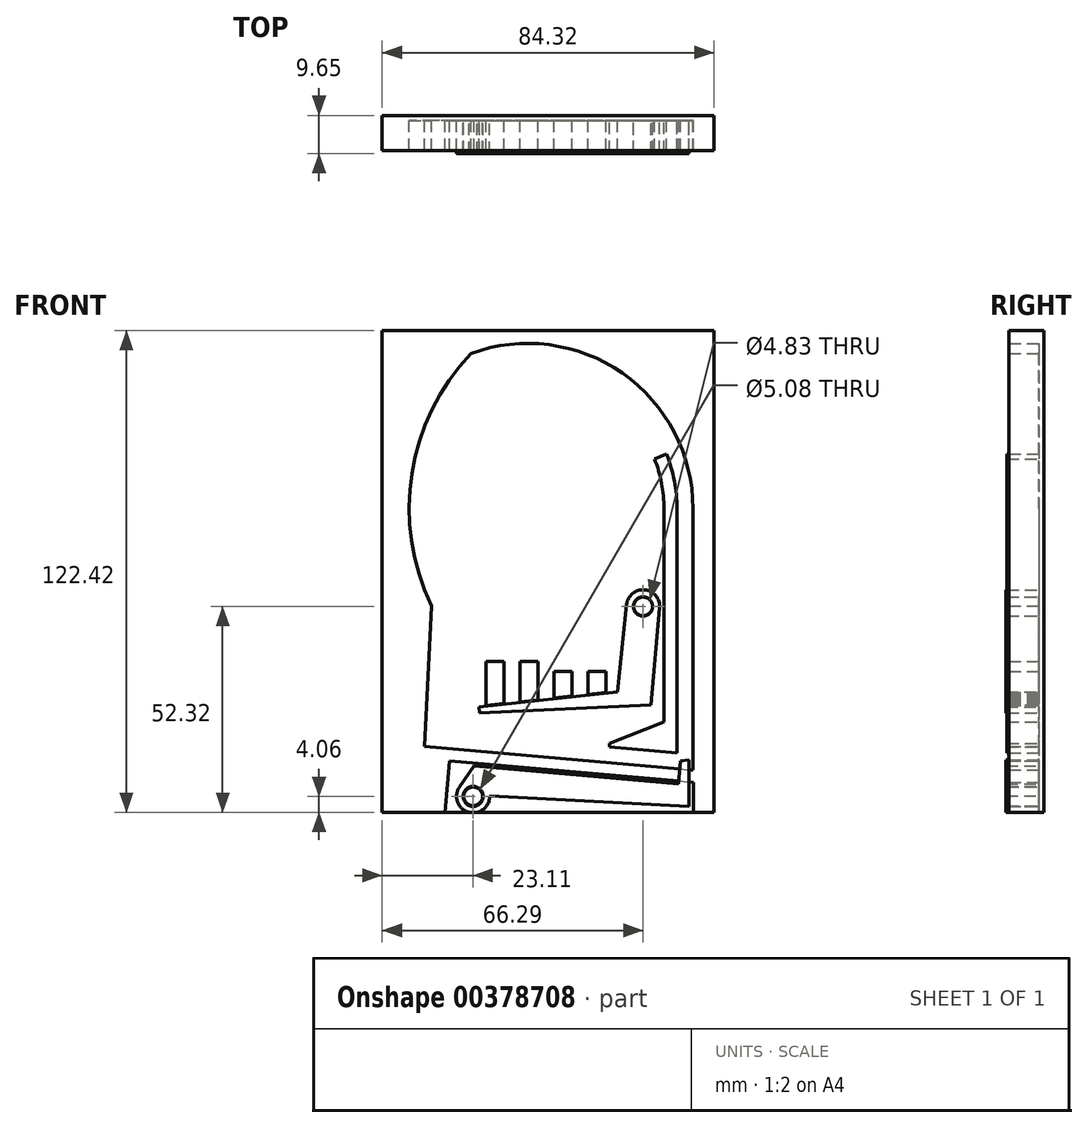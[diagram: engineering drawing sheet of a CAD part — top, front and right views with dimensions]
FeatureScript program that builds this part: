
annotation { "Feature Type Name" : "Feature", "Feature Type Description" : "" }
export const myFeature = defineFeature(function(context is Context, id is Id, definition is map)
    precondition{}
    {
        {
            var Q0;
            Q0=qCreatedBy(makeId("Front.planeOp"),FACE);
            var sketch = newSketch(context, id + "F0", { "sketchPlane" : qUnion([Q0])});
            skLineSegment(sketch, "E0.bottom", {"start": v(44.45, 63.5) * mm, "end": v(-44.45, 63.5) * mm});
            skLineSegment(sketch, "E0.top", {"start": v(44.45, -63.5) * mm, "end": v(-44.45, -63.5) * mm});
            skLineSegment(sketch, "E0.left", {"start": v(44.45, 63.5) * mm, "end": v(44.45, -63.5) * mm});
            skLineSegment(sketch, "E0.right", {"start": v(-44.45, 63.5) * mm, "end": v(-44.45, -63.5) * mm});
            skPoint(sketch, "E0.middle", {"position": v(0, 0) * mm});
            skLineSegment(sketch, "E1", {"start": v(-29.21, -42.66) * mm, "end": v(34.79, -48.26) * mm});
            skLineSegment(sketch, "E2", {"start": v(34.79, -48.26) * mm, "end": v(34.79, 15.95) * mm});
            skArc(sketch, "E3", {"start": v(34.79, 15.95) * mm, "mid": v(17.9, 48.57) * mm, "end": v(-18.48, 53.63) * mm});
            skArc(sketch, "E4", {"start": v(-18.48, 53.63) * mm, "mid": v(-32.67, 24.06) * mm, "end": v(-27.54, -8.34) * mm});
            skLineSegment(sketch, "E5", {"start": v(-27.54, -8.34) * mm, "end": v(-29.21, -42.66) * mm});
            skLineSegment(sketch, "E6", {"start": v(-17.78, -22.86) * mm, "end": v(-17.78, -30.48) * mm});
            skLineSegment(sketch, "E7", {"start": v(-9.14, -22.86) * mm, "end": v(-9.14, -33.34) * mm});
            skLineSegment(sketch, "E8", {"start": v(-0.5, -22.86) * mm, "end": v(-0.5, -32.39) * mm});
            skLineSegment(sketch, "E9", {"start": v(8.13, -22.86) * mm, "end": v(8.13, -31.43) * mm});
            skLineSegment(sketch, "E10", {"start": v(16.76, -22.86) * mm, "end": v(16.76, -30.48) * mm});
            skCircle(sketch, "E11", {"center": v(16.76, -30.48) * mm, "radius": 1.59 * mm});
            skLineSegment(sketch, "E12", {"start": v(16.76, -30.48) * mm, "end": v(-17.78, -34.3) * mm});
            skLineSegment(sketch, "E13", {"start": v(-17.78, -34.3) * mm, "end": v(-17.78, -30.48) * mm});
            skLineSegment(sketch, "E14", {"start": v(-28, -37.08) * mm, "end": v(-29.8, -37.08) * mm});
            skLineSegment(sketch, "E15", {"start": v(-17.78, -37.61) * mm, "end": v(26.76, -32.7) * mm});
            skLineSegment(sketch, "E16", {"start": v(26.76, -32.7) * mm, "end": v(24.13, -8.89) * mm});
            skLineSegment(sketch, "E17", {"start": v(-21.28, -49.63) * mm, "end": v(34.73, -55.5) * mm});
            skLineSegment(sketch, "E18", {"start": v(34.73, -55.5) * mm, "end": v(49.3, -48.12) * mm});
            skPoint(sketch, "E19", {"position": v(-19.05, -57.15) * mm});
            skSolve(sketch);
        }
        {
            var Q0;
            Q0=qCreatedBy(makeId("Front.planeOp"),FACE);
            cPlane(context, id + "F1", {"entities" : qUnion([Q0]), "cplaneType" : CPlaneType.OFFSET, "offset" : 6.35 * mm, "oppositeDirection" : true, "width" : 152.4 * mm, "height" : 152.4 * mm});
        }
        {
            var Q0;
            Q0=qCreatedBy(id+"F1.planeOp",FACE);
            var sketch = newSketch(context, id + "F2", { "sketchPlane" : qUnion([Q0])});
            skLineSegment(sketch, "E20.bottom", {"start": v(-42.16, 61.21) * mm, "end": v(42.16, 61.21) * mm});
            skLineSegment(sketch, "E20.top", {"start": v(-42.16, -61.21) * mm, "end": v(42.16, -61.21) * mm});
            skLineSegment(sketch, "E20.left", {"start": v(-42.16, 61.21) * mm, "end": v(-42.16, -61.21) * mm});
            skLineSegment(sketch, "E20.right", {"start": v(42.16, 61.21) * mm, "end": v(42.16, -61.21) * mm});
            skPoint(sketch, "E20.middle", {"position": v(0, 0) * mm});
            skLineSegment(sketch, "E21.0", {"start": v(44.45, 63.5) * mm, "end": v(-44.45, 63.5) * mm});
            skLineSegment(sketch, "E22.0", {"start": v(-44.45, 63.5) * mm, "end": v(-44.45, -63.5) * mm});
            skLineSegment(sketch, "E23.0", {"start": v(44.45, -63.5) * mm, "end": v(-44.45, -63.5) * mm});
            skLineSegment(sketch, "E24.0", {"start": v(44.45, 63.5) * mm, "end": v(44.45, -63.5) * mm});
            skSolve(sketch);
        }
        {
            var Q0;
            Q0=makeQuery(id+"F2.imprint","IMPRINT",FACE,{"disambiguationData":[TD([[makeQuery(id+"F2.imprint","IMPRINT",EDGE,{"derivedFrom":sQuery(id+"F2.wireOp",EDGE,"E20.bottom")}),-1.0]])]});
            extrude(context, id + "F3", {"entities" : qUnion([Q0]), "depth" : 1.27 * mm});
        }
        {
            var Q0;
            Q0=qCreatedBy(id+"F1.planeOp",FACE);
            var sketch = newSketch(context, id + "F4", { "sketchPlane" : qUnion([Q0])});
            skLineSegment(sketch, "E25.0", {"start": v(34.79, -48.26) * mm, "end": v(34.79, 15.95) * mm, "construction": true});
            skArc(sketch, "E26.0", {"start": v(34.79, 15.95) * mm, "mid": v(17.9, 48.57) * mm, "end": v(-18.48, 53.63) * mm, "construction": true});
            skArc(sketch, "E27.0", {"start": v(-18.48, 53.63) * mm, "mid": v(-32.67, 24.06) * mm, "end": v(-27.54, -8.34) * mm, "construction": true});
            skLineSegment(sketch, "E28.0", {"start": v(-27.54, -8.34) * mm, "end": v(-29.21, -42.66) * mm, "construction": true});
            skLineSegment(sketch, "E29.0", {"start": v(-29.21, -42.66) * mm, "end": v(34.79, -48.26) * mm, "construction": true});
            skLineSegment(sketch, "E30.0", {"start": v(44.45, 63.5) * mm, "end": v(-44.45, 63.5) * mm, "construction": true});
            skLineSegment(sketch, "E31.0", {"start": v(42.16, 61.21) * mm, "end": v(42.16, -61.21) * mm});
            skLineSegment(sketch, "E32.0", {"start": v(-42.16, 61.21) * mm, "end": v(42.16, 61.21) * mm});
            skLineSegment(sketch, "E33.0", {"start": v(-42.16, 61.21) * mm, "end": v(-42.16, -61.21) * mm});
            skLineSegment(sketch, "E34.0", {"start": v(-42.16, -61.21) * mm, "end": v(42.16, -61.21) * mm});
            skArc(sketch, "E35.0", {"start": v(36.82, 15.95) * mm, "mid": v(18.87, 50.38) * mm, "end": v(-19.63, 55.38) * mm});
            skLineSegment(sketch, "E35.1", {"start": v(36.82, -50.48) * mm, "end": v(36.82, 15.95) * mm});
            skArc(sketch, "E35.2", {"start": v(-19.63, 55.38) * mm, "mid": v(-34.6, 24.86) * mm, "end": v(-29.6, -8.76) * mm});
            skLineSegment(sketch, "E35.3", {"start": v(-29.6, -8.76) * mm, "end": v(-31.33, -44.51) * mm});
            skLineSegment(sketch, "E35.4", {"start": v(-31.33, -44.51) * mm, "end": v(36.82, -50.48) * mm});
            skLineSegment(sketch, "E36", {"start": v(-26.22, -61.21) * mm, "end": v(-25.07, -48.12) * mm});
            skLineSegment(sketch, "E37", {"start": v(-25.07, -48.12) * mm, "end": v(36.94, -53.55) * mm});
            skLineSegment(sketch, "E38", {"start": v(36.94, -53.55) * mm, "end": v(36.94, -61.21) * mm});
            skSolve(sketch);
        }
        {
            var Q0;
            {var subQ1=sQuery(id+"F4.wireOp",EDGE,"E31.0");Q0=makeQuery(id+"F4.imprint","IMPRINT",FACE,{"disambiguationData":[TD([[makeQuery(id+"F4.imprint","IMPRINT",EDGE,{"derivedFrom":subQ1}),-1.0]])]});}
            extrude(context, id + "F5", {"entities" : qUnion([Q0]), "operationType" : NewBodyOperationType.ADD, "depth" : 8.9 * mm});
        }
        {
            var Q0;
            Q0=qCreatedBy(id+"F1.planeOp",FACE);
            var sketch = newSketch(context, id + "F6", { "sketchPlane" : qUnion([Q0])});
            skArc(sketch, "E39.0", {"start": v(32.76, 15.95) * mm, "mid": v(32.1, 23.01) * mm, "end": v(30.12, 29.84) * mm});
            skLineSegment(sketch, "E39.1", {"start": v(32.76, -46.04) * mm, "end": v(32.76, 15.95) * mm});
            skPoint(sketch, "E40.0", {"position": v(24.13, -8.89) * mm});
            skCircle(sketch, "E41", {"center": v(24.13, -8.89) * mm, "radius": 2.39 * mm});
            skArc(sketch, "E42.0", {"start": v(29.46, 15.95) * mm, "mid": v(28.85, 22.4) * mm, "end": v(27.05, 28.63) * mm});
            skLineSegment(sketch, "E42.1", {"start": v(29.46, -45.75) * mm, "end": v(29.46, 15.95) * mm});
            skLineSegment(sketch, "E43", {"start": v(-5.18, 15.95) * mm, "end": v(30.12, 29.84) * mm});
            skLineSegment(sketch, "E44.0", {"start": v(15.56, -44.54) * mm, "end": v(32.76, -46.04) * mm});
            skLineSegment(sketch, "E45", {"start": v(15.56, -44.54) * mm, "end": v(15.63, -43.75) * mm});
            skLineSegment(sketch, "E46", {"start": v(15.63, -43.75) * mm, "end": v(29.46, -38.18) * mm});
            skPoint(sketch, "E47.0", {"position": v(-19.05, -57.15) * mm});
            skCircle(sketch, "E48", {"center": v(-19.05, -57.15) * mm, "radius": 2.39 * mm});
            skSolve(sketch);
        }
        {
            var Q0;
            {var subQ4=sQuery(id+"F6.wireOp",EDGE,"E45");Q0=makeQuery(id+"F6.imprint","IMPRINT",FACE,{"disambiguationData":[TD([[makeQuery(id+"F6.imprint","IMPRINT",EDGE,{"derivedFrom":subQ4}),-1.0]])]});}
            var Q1;
            {var subQ6=sQuery(id+"F6.wireOp",EDGE,"E39.0");Q1=makeQuery(id+"F6.imprint","IMPRINT",FACE,{"disambiguationData":[TD([[makeQuery(id+"F6.imprint","IMPRINT",EDGE,{"derivedFrom":subQ6}),1.0]])]});}
            var Q2;
            Q2=makeQuery(id+"F6.imprint","IMPRINT",FACE,{"disambiguationData":[TD([[makeQuery(id+"F6.imprint","IMPRINT",EDGE,{"derivedFrom":sQuery(id+"F6.wireOp",EDGE,"E41")}),1.0]])]});
            var Q3;
            Q3=makeQuery(id+"F6.imprint","IMPRINT",FACE,{"disambiguationData":[TD([[makeQuery(id+"F6.imprint","IMPRINT",EDGE,{"derivedFrom":sQuery(id+"F6.wireOp",EDGE,"E48")}),1.0]])]});
            extrude(context, id + "F7", {"entities" : qUnion([Q0, Q1, Q2, Q3]), "operationType" : NewBodyOperationType.ADD, "depth" : 9.4 * mm});
        }
        {
            var Q0;
            Q0=qCreatedBy(id+"F1.planeOp",FACE);
            var sketch = newSketch(context, id + "F8", { "sketchPlane" : qUnion([Q0])});
            skLineSegment(sketch, "E49.0", {"start": v(16.76, -22.86) * mm, "end": v(16.76, -30.48) * mm, "construction": true});
            skLineSegment(sketch, "E50.0", {"start": v(8.13, -22.86) * mm, "end": v(8.13, -31.43) * mm, "construction": true});
            skLineSegment(sketch, "E51.0", {"start": v(-0.5, -22.86) * mm, "end": v(-0.5, -32.39) * mm, "construction": true});
            skLineSegment(sketch, "E52.0", {"start": v(-9.14, -22.86) * mm, "end": v(-9.14, -33.34) * mm, "construction": true});
            skPoint(sketch, "E53.0", {"position": v(-17.78, -26.67) * mm});
            skLineSegment(sketch, "E54.0", {"start": v(-17.78, -22.86) * mm, "end": v(-17.78, -30.48) * mm, "construction": true});
            skLineSegment(sketch, "E55.0", {"start": v(-17.78, -34.3) * mm, "end": v(-17.78, -30.48) * mm, "construction": true});
            skLineSegment(sketch, "E56.0", {"start": v(14.73, -30.7) * mm, "end": v(10.16, -31.2) * mm});
            skLineSegment(sketch, "E57.0", {"start": v(-19.81, -34.51) * mm, "end": v(-19.81, -33.02) * mm});
            skLineSegment(sketch, "E57.1", {"start": v(-19.81, -25.4) * mm, "end": v(-19.81, -33.02) * mm});
            skLineSegment(sketch, "E58.0", {"start": v(-15.75, -34.07) * mm, "end": v(-15.75, -33.02) * mm});
            skLineSegment(sketch, "E58.1", {"start": v(-15.75, -22.86) * mm, "end": v(-15.75, -33.02) * mm});
            skLineSegment(sketch, "E59.0", {"start": v(-11.18, -22.86) * mm, "end": v(-11.18, -33.56) * mm});
            skLineSegment(sketch, "E60.0", {"start": v(-7.11, -22.86) * mm, "end": v(-7.11, -33.11) * mm});
            skArc(sketch, "E61.0", {"start": v(-19.63, 55.38) * mm, "mid": v(-34.6, 24.86) * mm, "end": v(-29.6, -8.76) * mm});
            skLineSegment(sketch, "E61.1", {"start": v(-30.97, -36.98) * mm, "end": v(-31.33, -44.51) * mm});
            skLineSegment(sketch, "E61.2", {"start": v(-31.33, -44.51) * mm, "end": v(36.82, -50.48) * mm});
            skLineSegment(sketch, "E61.3", {"start": v(-29.6, -8.76) * mm, "end": v(-30.97, -36.98) * mm});
            skLineSegment(sketch, "E61.4", {"start": v(36.82, -50.48) * mm, "end": v(36.82, 15.95) * mm});
            skArc(sketch, "E61.5", {"start": v(36.82, 15.95) * mm, "mid": v(18.87, 50.38) * mm, "end": v(-19.63, 55.38) * mm});
            skLineSegment(sketch, "E62.0", {"start": v(-2.54, -22.86) * mm, "end": v(-2.54, -32.6) * mm});
            skLineSegment(sketch, "E63.0", {"start": v(1.52, -25.4) * mm, "end": v(1.52, -32.16) * mm});
            skLineSegment(sketch, "E64.0", {"start": v(6.1, -25.4) * mm, "end": v(6.1, -31.66) * mm});
            skLineSegment(sketch, "E65.0", {"start": v(10.16, -25.4) * mm, "end": v(10.16, -31.2) * mm});
            skLineSegment(sketch, "E66.0", {"start": v(14.73, -25.4) * mm, "end": v(14.73, -30.7) * mm});
            skLineSegment(sketch, "E67.0", {"start": v(18.8, -25.4) * mm, "end": v(18.8, -30.26) * mm});
            skLineSegment(sketch, "E68", {"start": v(-7.11, -22.86) * mm, "end": v(-2.54, -22.86) * mm});
            skLineSegment(sketch, "E69", {"start": v(1.52, -25.4) * mm, "end": v(6.1, -25.4) * mm});
            skLineSegment(sketch, "E70", {"start": v(10.16, -25.4) * mm, "end": v(14.73, -25.4) * mm});
            skPoint(sketch, "E71.orphan", {"position": v(-17.78, -34.3) * mm});
            skLineSegment(sketch, "E72.trimOffspring", {"start": v(-11.18, -33.56) * mm, "end": v(-15.75, -34.07) * mm});
            skLineSegment(sketch, "E73.trimOffspring", {"start": v(-2.54, -32.6) * mm, "end": v(-7.11, -33.11) * mm});
            skLineSegment(sketch, "E74.trimOffspring", {"start": v(6.1, -31.66) * mm, "end": v(1.52, -32.16) * mm});
            skPoint(sketch, "E75.orphan", {"position": v(16.76, -30.48) * mm});
            skLineSegment(sketch, "E76", {"start": v(-15.75, -22.86) * mm, "end": v(-11.18, -22.86) * mm});
            skSolve(sketch);
        }
        {
            var Q0;
            Q0=makeQuery(id+"F8.imprint","IMPRINT",FACE,{"disambiguationData":[TD([[makeQuery(id+"F8.imprint","IMPRINT",EDGE,{"derivedFrom":sQuery(id+"F8.wireOp",EDGE,"E58.0")}),-1.0]])]});
            var Q1;
            Q1=makeQuery(id+"F8.imprint","IMPRINT",FACE,{"disambiguationData":[TD([[makeQuery(id+"F8.imprint","IMPRINT",EDGE,{"derivedFrom":sQuery(id+"F8.wireOp",EDGE,"E60.0")}),1.0]])]});
            var Q2;
            Q2=makeQuery(id+"F8.imprint","IMPRINT",FACE,{"disambiguationData":[TD([[makeQuery(id+"F8.imprint","IMPRINT",EDGE,{"derivedFrom":sQuery(id+"F8.wireOp",EDGE,"E63.0")}),1.0]])]});
            var Q3;
            Q3=makeQuery(id+"F8.imprint","IMPRINT",FACE,{"disambiguationData":[TD([[makeQuery(id+"F8.imprint","IMPRINT",EDGE,{"derivedFrom":sQuery(id+"F8.wireOp",EDGE,"E56.0")}),-1.0]])]});
            extrude(context, id + "F9", {"entities" : qUnion([Q0, Q1, Q2, Q3]), "operationType" : NewBodyOperationType.ADD, "depth" : 8.9 * mm});
        }
        {
            var Q0;
            Q0=makeQuery(id+"F5.boolean.opBoolean","SPLIT",FACE,{"disambiguationData":[TD([makeQuery(id+"F5.opExtrude","SWEPT_FACE",FACE,{"disambiguationData":[OSD([sQuery(id+"F4.wireOp",EDGE,"E35.0")])]})])],"derivedFrom":makeQuery(id+"F3.opExtrude","CAP_FACE",FACE,{"disambiguationData":[OSD([sQuery(id+"F2.wireOp",EDGE,"E20.bottom"),sQuery(id+"F2.wireOp",EDGE,"E20.top"),sQuery(id+"F2.wireOp",EDGE,"E20.left"),sQuery(id+"F2.wireOp",EDGE,"E20.right")])],"isStart":false})});
            var sketch = newSketch(context, id + "F10", { "sketchPlane" : qUnion([Q0])});
            skCircle(sketch, "E77", {"center": v(24.13, -8.89) * mm, "radius": 2.41 * mm});
            skCircle(sketch, "E78", {"center": v(24.13, -8.89) * mm, "radius": 4.22 * mm});
            skLineSegment(sketch, "E79", {"start": v(19.93, -8.44) * mm, "end": v(17.59, -30.56) * mm});
            skLineSegment(sketch, "E80", {"start": v(17.59, -30.56) * mm, "end": v(-17.53, -34.43) * mm});
            skLineSegment(sketch, "E81", {"start": v(-17.53, -34.43) * mm, "end": v(-17.36, -36) * mm});
            skLineSegment(sketch, "E82", {"start": v(-17.36, -36) * mm, "end": v(26.18, -33.87) * mm});
            skLineSegment(sketch, "E83", {"start": v(26.18, -33.87) * mm, "end": v(28.33, -9.26) * mm});
            skLineSegment(sketch, "E84.0", {"start": v(-11.18, -33.56) * mm, "end": v(-15.75, -34.07) * mm});
            skLineSegment(sketch, "E85", {"start": v(24.13, -8.89) * mm, "end": v(24.13, -17.24) * mm});
            skSolve(sketch);
        }
        {
            var Q0;
            {var subQ0=sQuery(id+"F10.wireOp",EDGE,"E79");Q0=makeQuery(id+"F10.imprint","IMPRINT",FACE,{"disambiguationData":[TD([[makeQuery(id+"F10.imprint","IMPRINT",EDGE,{"derivedFrom":subQ0}),1.0]])]});}
            var Q1;
            Q1=makeQuery(id+"F10.imprint","IMPRINT",FACE,{"disambiguationData":[TD([[makeQuery(id+"F10.imprint","IMPRINT",EDGE,{"derivedFrom":sQuery(id+"F10.wireOp",EDGE,"E77")}),-1.0]])]});
            extrude(context, id + "F11", {"entities" : qUnion([Q0, Q1]), "depth" : 8.38 * mm});
        }
        {
            var Q0;
            {var subQ3=sQuery(id+"F2.wireOp",EDGE,"E20.top");Q0=makeQuery(id+"F5.boolean.opBoolean","SPLIT",FACE,{"disambiguationData":[TD([makeQuery(id+"F3.opExtrude","SWEPT_FACE",FACE,{"disambiguationData":[OSD([subQ3])]})])],"derivedFrom":makeQuery(id+"F3.opExtrude","CAP_FACE",FACE,{"disambiguationData":[OSD([sQuery(id+"F2.wireOp",EDGE,"E20.bottom"),subQ3,sQuery(id+"F2.wireOp",EDGE,"E20.left"),sQuery(id+"F2.wireOp",EDGE,"E20.right")])],"isStart":false})});}
            var sketch = newSketch(context, id + "F12", { "sketchPlane" : qUnion([Q0])});
            skCircle(sketch, "E86", {"center": v(-19.05, -57.15) * mm, "radius": 4.2 * mm});
            skCircle(sketch, "E87", {"center": v(-19.05, -57.15) * mm, "radius": 2.54 * mm});
            skLineSegment(sketch, "E88", {"start": v(-22.48, -54.75) * mm, "end": v(-18.77, -49.44) * mm});
            skLineSegment(sketch, "E89", {"start": v(-18.77, -49.44) * mm, "end": v(33.08, -53.97) * mm});
            skLineSegment(sketch, "E90", {"start": v(33.08, -53.97) * mm, "end": v(33.59, -48.12) * mm});
            skLineSegment(sketch, "E91", {"start": v(33.59, -48.12) * mm, "end": v(35.84, -47.92) * mm});
            skLineSegment(sketch, "E92", {"start": v(35.84, -47.92) * mm, "end": v(35.84, -59.64) * mm});
            skLineSegment(sketch, "E93", {"start": v(35.84, -59.64) * mm, "end": v(-14.86, -57.01) * mm});
            skSolve(sketch);
        }
        {
            var Q0;
            {var subQ4=sQuery(id+"F12.wireOp",EDGE,"E88");Q0=makeQuery(id+"F12.imprint","IMPRINT",FACE,{"disambiguationData":[TD([[makeQuery(id+"F12.imprint","IMPRINT",EDGE,{"derivedFrom":subQ4}),-1.0]])]});}
            var Q1;
            {var subQ0=sQuery(id+"F12.wireOp",EDGE,"E91");Q1=makeQuery(id+"F12.imprint","IMPRINT",FACE,{"disambiguationData":[TD([[makeQuery(id+"F12.imprint","IMPRINT",EDGE,{"derivedFrom":subQ0}),-1.0]])]});}
            var Q2;
            Q2=makeQuery(id+"F12.imprint","IMPRINT",FACE,{"disambiguationData":[TD([[makeQuery(id+"F12.imprint","IMPRINT",EDGE,{"derivedFrom":sQuery(id+"F12.wireOp",EDGE,"E87")}),-1.0]])]});
            var Q3;
            {var subQ0=sQuery(id+"F12.wireOp",EDGE,"E86");var subQ1=makeQuery(id+"F3.opExtrude","CAP_EDGE",EDGE,{"disambiguationData":[OSD([sQuery(id+"F2.wireOp",EDGE,"E20.top")])],"isStart":false});var subQ2=makeQuery(id+"F12.imprint","INTERSECT",VERTEX,{"disambiguationData":[OD(0.0)],"derivedFrom":[subQ1,subQ0]});Q3=makeQuery(id+"F12.imprint","IMPRINT",FACE,{"disambiguationData":[TD([[makeQuery(id+"F12.imprint","IMPRINT",EDGE,{"disambiguationData":[TD([[subQ2,-1.0]])],"derivedFrom":subQ0}),1.0]])]});}
            extrude(context, id + "F13", {"entities" : qUnion([Q0, Q1, Q2, Q3]), "depth" : 8.38 * mm});
        }
    });
